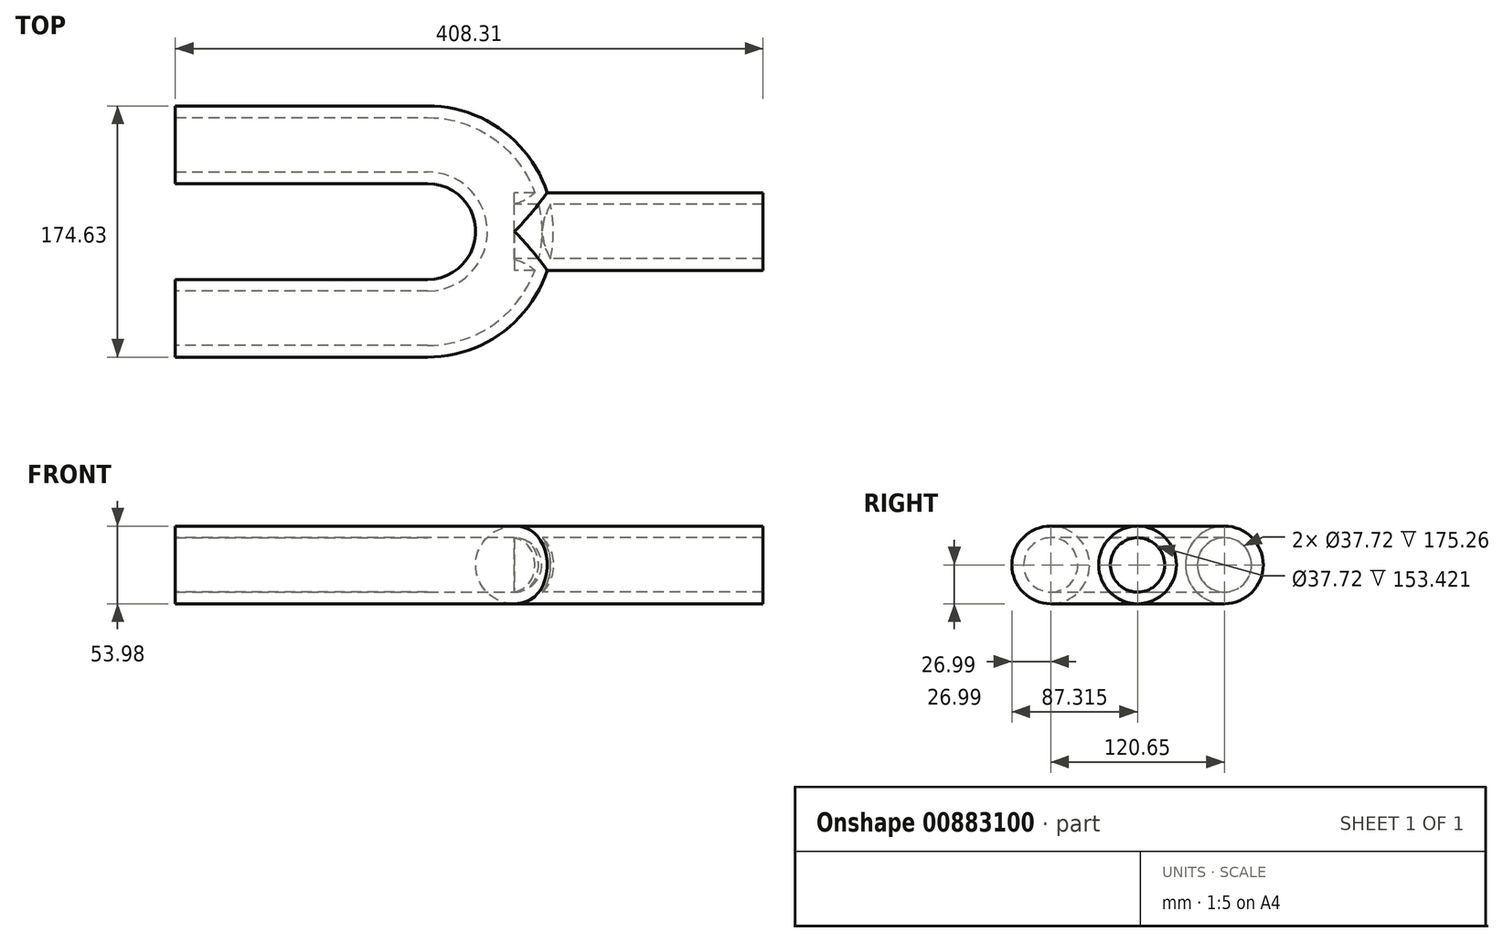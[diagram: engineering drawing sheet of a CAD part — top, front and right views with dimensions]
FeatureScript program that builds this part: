
annotation { "Feature Type Name" : "Feature", "Feature Type Description" : "" }
export const myFeature = defineFeature(function(context is Context, id is Id, definition is map)
    precondition{}
    {
        {
            var Q0;
            Q0=qCreatedBy(makeId("Front.planeOp"),FACE);
            var sketch = newSketch(context, id + "F0", { "sketchPlane" : qUnion([Q0])});
            skLineSegment(sketch, "E0", {"start": v(0, 125.41) * mm, "end": v(0, 609.6) * mm});
            skLineSegment(sketch, "E1", {"start": v(125.41, 0) * mm, "end": v(304.8, 0) * mm});
            skPoint(sketch, "E2.visualSharp", {"position": v(0, 0) * mm});
            skArc(sketch, "E3.filletArc", {"start": v(0, 125.41) * mm, "mid": v(36.73, 36.73) * mm, "end": v(125.41, 0) * mm});
            skSolve(sketch);
        }
        {
            var Q0;
            Q0=qCreatedBy(makeId("Front.planeOp"),FACE);
            cPlane(context, id + "F1", {"entities" : qUnion([Q0]), "cplaneType" : CPlaneType.OFFSET, "offset" : 120.65 * mm, "width" : 152.4 * mm, "height" : 152.4 * mm});
        }
        {
            var Q0;
            Q0=qCreatedBy(id+"F1.planeOp",FACE);
            var sketch = newSketch(context, id + "F2", { "sketchPlane" : qUnion([Q0])});
            skLineSegment(sketch, "E4.0", {"start": v(125.41, 0) * mm, "end": v(304.8, 0) * mm});
            skArc(sketch, "E4.1", {"start": v(0, 125.41) * mm, "mid": v(36.73, 36.73) * mm, "end": v(125.41, 0) * mm});
            skLineSegment(sketch, "E4.2", {"start": v(0, 125.41) * mm, "end": v(0, 609.6) * mm});
            skSolve(sketch);
        }
        {
            var Q0;
            Q0=qCreatedBy(makeId("Top.planeOp"),FACE);
            var sketch = newSketch(context, id + "F3", { "sketchPlane" : qUnion([Q0])});
            skPoint(sketch, "E5.0", {"position": v(304.8, -120.65) * mm});
            skPoint(sketch, "E5.1", {"position": v(304.8, 0) * mm});
            skArc(sketch, "E6", {"start": v(304.8, -120.65) * mm, "mid": v(365.13, -60.33) * mm, "end": v(304.8, 0) * mm});
            skLineSegment(sketch, "E7", {"start": v(304.8, -120.65) * mm, "end": v(304.8, 0) * mm, "construction": true});
            skPoint(sketch, "E8", {"position": v(365.13, -60.32) * mm});
            skSolve(sketch);
        }
        {
            var Q0;
            Q0=sQuery(id+"F2.wireOp",VERTEX,"E4.2.end");
            var Q1;
            Q1=qCreatedBy(makeId("Top.planeOp"),FACE);
            cPlane(context, id + "F4", {"entities" : qUnion([Q0, Q1]), "cplaneType" : CPlaneType.PLANE_POINT, "offset" : 25.4 * mm, "width" : 152.4 * mm, "height" : 152.4 * mm});
        }
        {
            var Q0;
            Q0=qCreatedBy(id+"F4.planeOp",FACE);
            var sketch = newSketch(context, id + "F5", { "sketchPlane" : qUnion([Q0])});
            skCircle(sketch, "E9", {"center": v(0, 0) * mm, "radius": 18.86 * mm});
            skCircle(sketch, "E10", {"center": v(0, 0) * mm, "radius": 26.99 * mm});
            skSolve(sketch);
        }
        {
            var Q0;
            Q0=makeQuery(id+"F5.imprint","IMPRINT",FACE,{"disambiguationData":[TD([[makeQuery(id+"F5.imprint","IMPRINT",EDGE,{"derivedFrom":sQuery(id+"F5.wireOp",EDGE,"E9")}),-1.0]])]});
            var Q1;
            Q1=sQuery(id+"F0.wireOp",EDGE,"E0");
            var Q2;
            Q2=sQuery(id+"F0.wireOp",EDGE,"E3.filletArc");
            var Q3;
            Q3=sQuery(id+"F0.wireOp",EDGE,"E1");
            var Q4;
            Q4=sQuery(id+"F3.wireOp",EDGE,"E6");
            var Q5;
            Q5=sQuery(id+"F2.wireOp",EDGE,"E4.0");
            var Q6;
            Q6=sQuery(id+"F2.wireOp",EDGE,"E4.1");
            var Q7;
            Q7=sQuery(id+"F2.wireOp",EDGE,"E4.2");
            sweep(context, id + "F6", {"profiles" : qUnion([Q0]), "path" : qUnion([Q1, Q2, Q3, Q4, Q5, Q6, Q7])});
        }
        {
            var Q0;
            Q0=qCreatedBy(makeId("Top.planeOp"),FACE);
            var sketch = newSketch(context, id + "F7", { "sketchPlane" : qUnion([Q0])});
            skPoint(sketch, "E11.0", {"position": v(365.13, -60.32) * mm});
            skLineSegment(sketch, "E12", {"start": v(365.12, -60.32) * mm, "end": v(3717.93, -60.32) * mm});
            skSolve(sketch);
        }
        {
            var Q0;
            Q0=sQuery(id+"F7.wireOp",VERTEX,"E12.end");
            var Q1;
            Q1=qCreatedBy(makeId("Right.planeOp"),FACE);
            cPlane(context, id + "F8", {"entities" : qUnion([Q0, Q1]), "cplaneType" : CPlaneType.PLANE_POINT, "offset" : 25.4 * mm, "width" : 152.4 * mm, "height" : 152.4 * mm});
        }
        {
            var Q0;
            Q0=qCreatedBy(id+"F8.planeOp",FACE);
            var sketch = newSketch(context, id + "F9", { "sketchPlane" : qUnion([Q0])});
            skPoint(sketch, "E13.0", {"position": v(-60.32, 0) * mm});
            skCircle(sketch, "E14", {"center": v(-60.32, 0) * mm, "radius": 18.86 * mm});
            skCircle(sketch, "E15", {"center": v(-60.32, 0) * mm, "radius": 26.99 * mm});
            skSolve(sketch);
        }
        {
            var Q0;
            Q0=makeQuery(id+"F9.imprint","IMPRINT",FACE,{"disambiguationData":[TD([[makeQuery(id+"F9.imprint","IMPRINT",EDGE,{"derivedFrom":sQuery(id+"F9.wireOp",EDGE,"E14")}),-1.0]])]});
            var Q1;
            Q1=sQuery(id+"F7.wireOp",EDGE,"E12");
            sweep(context, id + "F10", {"operationType" : NewBodyOperationType.ADD, "profiles" : qUnion([Q0]), "path" : qUnion([Q1])});
        }
        {
            var Q0;
            Q0=qCreatedBy(makeId("Right.planeOp"),FACE);
            var sketch = newSketch(context, id + "F11", { "sketchPlane" : qUnion([Q0])});
            skLineSegment(sketch, "E16.bottom", {"start": v(385.43, 813.1) * mm, "end": v(-485.37, 813.1) * mm});
            skLineSegment(sketch, "E16.top", {"start": v(385.43, -135.36) * mm, "end": v(-485.37, -135.36) * mm});
            skLineSegment(sketch, "E16.left", {"start": v(385.43, 813.1) * mm, "end": v(385.43, -135.36) * mm});
            skLineSegment(sketch, "E16.right", {"start": v(-485.37, 813.1) * mm, "end": v(-485.37, -135.36) * mm});
            skSolve(sketch);
        }
        {
            var Q0;
            Q0 = qSketchRegion(id + "F11", true);
            extrude(context, id + "F12", {"entities" : qUnion([Q0]), "operationType" : NewBodyOperationType.REMOVE, "depth" : 129.54 * mm, "offsetDistance" : 25.4 * mm, "hasSecondDirection" : true, "secondDirectionOppositeDirection" : true, "secondDirectionDepth" : 101.6 * mm});
        }
        {
            var Q0;
            Q0=qCreatedBy(id+"F8.planeOp",FACE);
            var sketch = newSketch(context, id + "F13", { "sketchPlane" : qUnion([Q0])});
            skLineSegment(sketch, "E17.bottom", {"start": v(-385.38, -294.35) * mm, "end": v(143.68, -294.35) * mm});
            skLineSegment(sketch, "E17.top", {"start": v(-385.38, 172.59) * mm, "end": v(143.68, 172.59) * mm});
            skLineSegment(sketch, "E17.left", {"start": v(-385.38, -294.35) * mm, "end": v(-385.38, 172.59) * mm});
            skLineSegment(sketch, "E17.right", {"start": v(143.68, -294.35) * mm, "end": v(143.68, 172.59) * mm});
            skSolve(sketch);
        }
        {
            var Q0;
            Q0 = qSketchRegion(id + "F13", true);
            extrude(context, id + "F14", {"entities" : qUnion([Q0]), "operationType" : NewBodyOperationType.REMOVE, "oppositeDirection" : true, "depth" : 3180.08 * mm, "offsetDistance" : 25.4 * mm});
        }
    });
